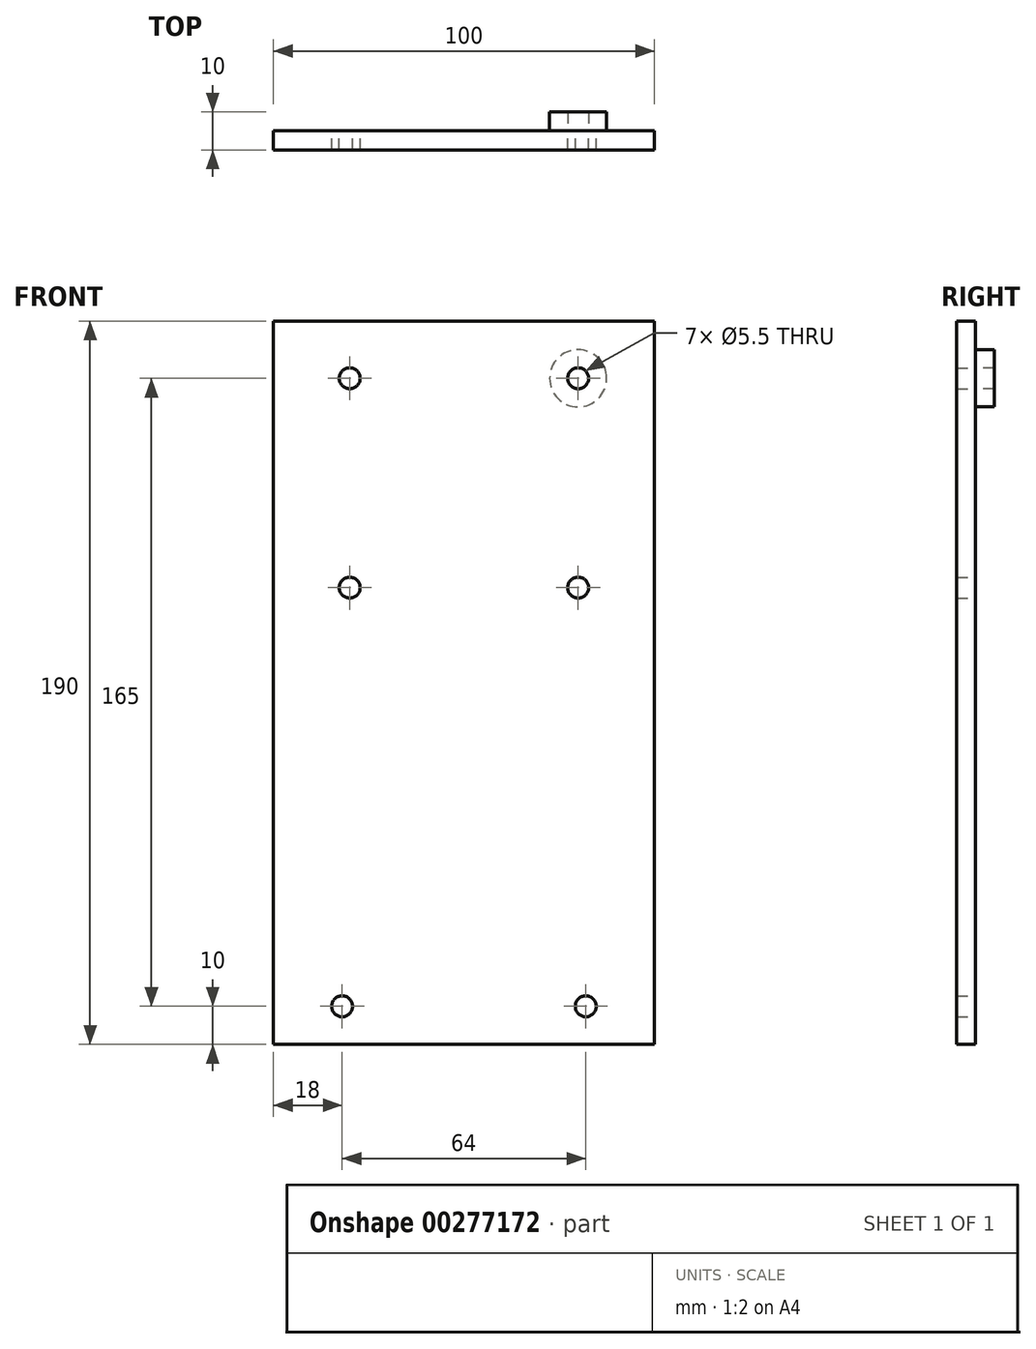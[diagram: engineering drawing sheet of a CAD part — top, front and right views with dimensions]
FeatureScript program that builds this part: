
annotation { "Feature Type Name" : "Feature", "Feature Type Description" : "" }
export const myFeature = defineFeature(function(context is Context, id is Id, definition is map)
    precondition{}
    {
        {
            var Q0;
            Q0=qCreatedBy(makeId("Front.planeOp"),FACE);
            var sketch = newSketch(context, id + "F0", { "sketchPlane" : qUnion([Q0])});
            skLineSegment(sketch, "E0.bottom", {"start": v(50, 95) * mm, "end": v(-50, 95) * mm});
            skLineSegment(sketch, "E0.top", {"start": v(50, -95) * mm, "end": v(-50, -95) * mm});
            skLineSegment(sketch, "E0.left", {"start": v(50, 95) * mm, "end": v(50, -95) * mm});
            skLineSegment(sketch, "E0.right", {"start": v(-50, 95) * mm, "end": v(-50, -95) * mm});
            skPoint(sketch, "E0.middle", {"position": v(0, 0) * mm});
            skCircle(sketch, "E1", {"center": v(-30, 80) * mm, "radius": 2.75 * mm});
            skCircle(sketch, "E2", {"center": v(30, 80) * mm, "radius": 2.75 * mm});
            skCircle(sketch, "E3", {"center": v(-30, 25) * mm, "radius": 2.75 * mm});
            skCircle(sketch, "E4", {"center": v(30, 25) * mm, "radius": 2.75 * mm});
            skCircle(sketch, "E5", {"center": v(-32, -85) * mm, "radius": 2.75 * mm});
            skCircle(sketch, "E6", {"center": v(32, -85) * mm, "radius": 2.75 * mm});
            skSolve(sketch);
        }
        {
            var Q0;
            Q0=makeQuery(id+"F0.imprint","IMPRINT",FACE,{"disambiguationData":[TD([[makeQuery(id+"F0.imprint","IMPRINT",EDGE,{"derivedFrom":sQuery(id+"F0.wireOp",EDGE,"E0.bottom")}),1.0]])]});
            extrude(context, id + "F1", {"entities" : qUnion([Q0]), "depth" : 5 * mm});
        }
        {
            var Q0;
            Q0=makeQuery(id+"F1.opExtrude","CAP_FACE",FACE,{"disambiguationData":[OSD([sQuery(id+"F0.wireOp",EDGE,"E0.bottom"),sQuery(id+"F0.wireOp",EDGE,"E0.top"),sQuery(id+"F0.wireOp",EDGE,"E0.left"),sQuery(id+"F0.wireOp",EDGE,"E0.right"),sQuery(id+"F0.wireOp",EDGE,"E1"),sQuery(id+"F0.wireOp",EDGE,"E2"),sQuery(id+"F0.wireOp",EDGE,"E3"),sQuery(id+"F0.wireOp",EDGE,"E4"),sQuery(id+"F0.wireOp",EDGE,"E5"),sQuery(id+"F0.wireOp",EDGE,"E6")])],"isStart":true});
            var sketch = newSketch(context, id + "F2", { "sketchPlane" : qUnion([Q0])});
            skSolve(sketch);
        }
        {
            var Q0;
            Q0=makeQuery(id+"F2.imprint","IMPRINT",FACE,{"disambiguationData":[TD([[makeQuery(id+"F2.imprint","IMPRINT",EDGE,{"derivedFrom":makeQuery(id+"F1.opExtrude","CAP_EDGE",EDGE,{"disambiguationData":[OSD([sQuery(id+"F0.wireOp",EDGE,"E0.bottom")])],"isStart":true})}),-1.0]])]});
            var sketch = newSketch(context, id + "F3", { "sketchPlane" : qUnion([Q0])});
            skCircle(sketch, "E7", {"center": v(-30, 80) * mm, "radius": 7.5 * mm});
            skSolve(sketch);
        }
        {
            var Q0;
            Q0=makeQuery(id+"F3.imprint","IMPRINT",FACE,{"disambiguationData":[TD([[makeQuery(id+"F3.imprint","IMPRINT",EDGE,{"derivedFrom":sQuery(id+"F3.wireOp",EDGE,"E7")}),1.0]])]});
            extrude(context, id + "F4", {"entities" : qUnion([Q0]), "depth" : 5 * mm});
        }
    });
